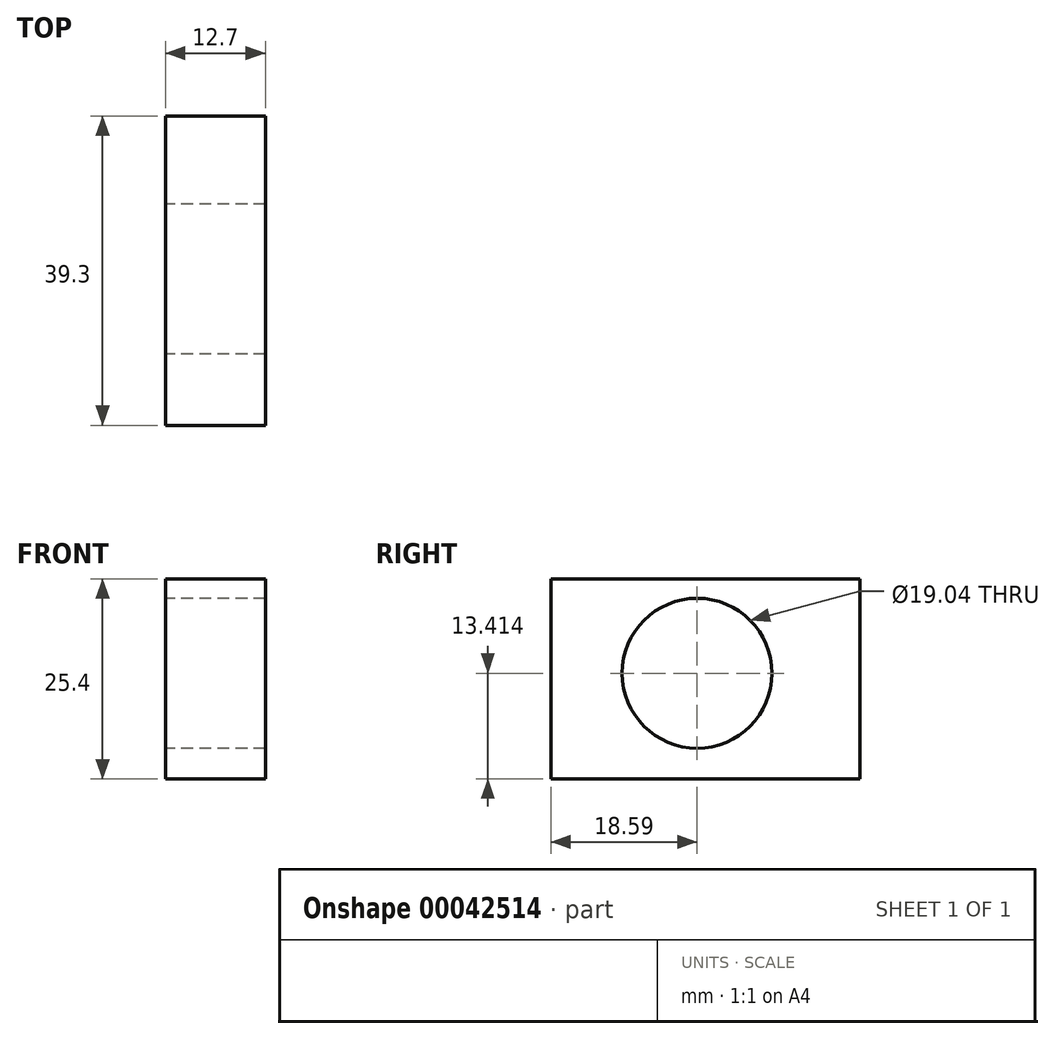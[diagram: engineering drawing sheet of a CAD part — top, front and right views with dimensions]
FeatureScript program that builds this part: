
annotation { "Feature Type Name" : "Feature", "Feature Type Description" : "" }
export const myFeature = defineFeature(function(context is Context, id is Id, definition is map)
    precondition{}
    {
        {
            var Q0;
            Q0=qCreatedBy(makeId("Right.planeOp"),FACE);
            var sketch = newSketch(context, id + "F0", { "sketchPlane" : qUnion([Q0])});
            skLineSegment(sketch, "E0.bottom", {"start": v(-13, 0) * mm, "end": v(26.3, 0) * mm});
            skLineSegment(sketch, "E0.top", {"start": v(-13, -25.4) * mm, "end": v(26.3, -25.4) * mm});
            skLineSegment(sketch, "E0.left", {"start": v(-13, 0) * mm, "end": v(-13, -25.4) * mm});
            skLineSegment(sketch, "E0.right", {"start": v(26.3, 0) * mm, "end": v(26.3, -25.4) * mm});
            skCircle(sketch, "E1", {"center": v(5.6, -11.99) * mm, "radius": 9.52 * mm});
            skSolve(sketch);
        }
        {
            var Q0;
            Q0 = qSketchRegion(id + "F0", true);
            extrude(context, id + "F1", {"entities" : qUnion([Q0]), "depth" : 12.7 * mm});
        }
    });
